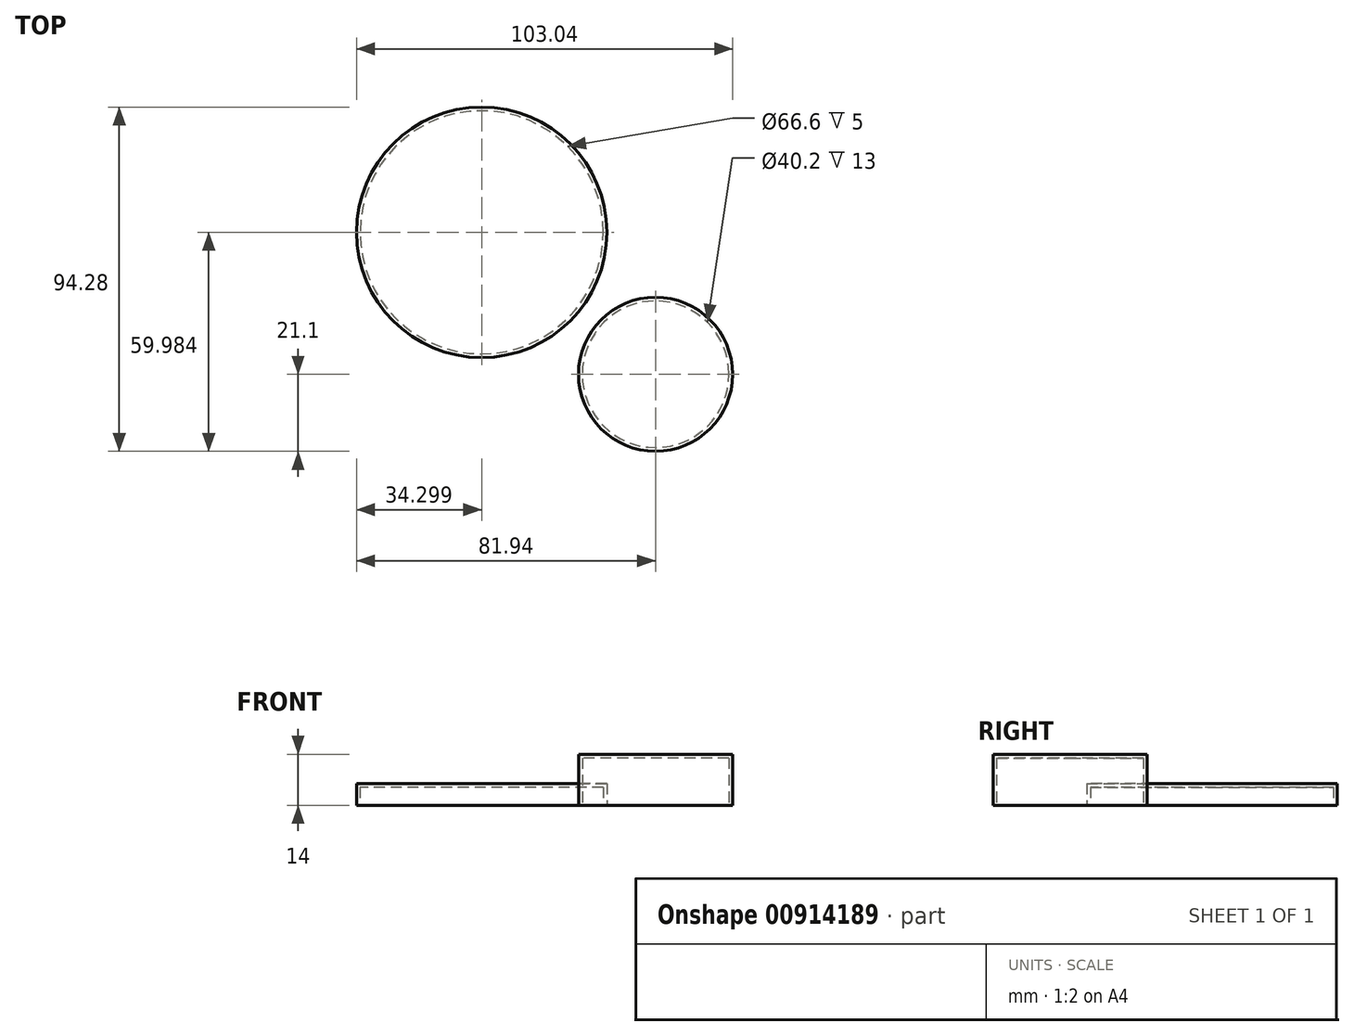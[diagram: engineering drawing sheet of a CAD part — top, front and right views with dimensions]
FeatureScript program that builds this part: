
annotation { "Feature Type Name" : "Feature", "Feature Type Description" : "" }
export const myFeature = defineFeature(function(context is Context, id is Id, definition is map)
    precondition{}
    {
        {
            assignVariable(context, id + "F0", {"name" : "height", "anyValue" : 14});
        }
        {
            assignVariable(context, id + "F1", {"name" : "height2", "anyValue" : 6});
        }
        {
            var Q0;
            Q0=qCreatedBy(makeId("Top.planeOp"),FACE);
            var sketch = newSketch(context, id + "F2", { "sketchPlane" : qUnion([Q0])});
            skCircle(sketch, "E0", {"center": v(0, 0) * mm, "radius": 20.1 * mm});
            skCircle(sketch, "E1", {"center": v(0, 0) * mm, "radius": 21.1 * mm});
            skLineSegment(sketch, "E2", {"start": v(0, 20.1) * mm, "end": v(0, 21.1) * mm, "construction": true});
            skCircle(sketch, "E3", {"center": v(-47.64, 38.88) * mm, "radius": 33.3 * mm});
            skCircle(sketch, "E4", {"center": v(-47.64, 38.88) * mm, "radius": 34.3 * mm});
            skLineSegment(sketch, "E5", {"start": v(-47.64, 72.18) * mm, "end": v(-47.64, 73.18) * mm, "construction": true});
            skSolve(sketch);
        }
        {
            var Q0;
            Q0=makeQuery(id+"F2.imprint","IMPRINT",FACE,{"disambiguationData":[TD([[makeQuery(id+"F2.imprint","IMPRINT",EDGE,{"derivedFrom":sQuery(id+"F2.wireOp",EDGE,"E0")}),-1.0]])]});
            var Q1;
            Q1=makeQuery(id+"F2.imprint","IMPRINT",FACE,{"disambiguationData":[TD([[makeQuery(id+"F2.imprint","IMPRINT",EDGE,{"derivedFrom":sQuery(id+"F2.wireOp",EDGE,"E0")}),1.0]])]});
            extrude(context, id + "F3", {"entities" : qUnion([Q0, Q1]), "depth" : (getVariable(context, 'height')) * mm, "offsetDistance" : 25 * mm});
        }
        {
            var Q0;
            Q0=makeQuery(id+"F2.imprint","IMPRINT",FACE,{"disambiguationData":[TD([[makeQuery(id+"F2.imprint","IMPRINT",EDGE,{"derivedFrom":sQuery(id+"F2.wireOp",EDGE,"E0")}),1.0]])]});
            extrude(context, id + "F4", {"entities" : qUnion([Q0]), "operationType" : NewBodyOperationType.REMOVE, "depth" : (getVariable(context, 'height') - 1) * mm, "offsetDistance" : 25 * mm});
        }
        {
            var Q0;
            Q0=makeQuery(id+"F2.imprint","IMPRINT",FACE,{"disambiguationData":[TD([[makeQuery(id+"F2.imprint","IMPRINT",EDGE,{"derivedFrom":sQuery(id+"F2.wireOp",EDGE,"E3")}),1.0]])]});
            var Q1;
            Q1=makeQuery(id+"F2.imprint","IMPRINT",FACE,{"disambiguationData":[TD([[makeQuery(id+"F2.imprint","IMPRINT",EDGE,{"derivedFrom":sQuery(id+"F2.wireOp",EDGE,"E3")}),-1.0]])]});
            var Q2;
            Q2=makeQuery(id+"F2.imprint","IMPRINT",FACE,{"disambiguationData":[TD([[makeQuery(id+"F2.imprint","IMPRINT",EDGE,{"derivedFrom":sQuery(id+"F2.wireOp",EDGE,"E3")}),1.0]])]});
            var Q3;
            Q3=makeQuery(id+"F2.imprint","IMPRINT",FACE,{"disambiguationData":[TD([[makeQuery(id+"F2.imprint","IMPRINT",EDGE,{"derivedFrom":sQuery(id+"F2.wireOp",EDGE,"E3")}),-1.0]])]});
            extrude(context, id + "F5", {"entities" : qUnion([Q0, Q1, Q2, Q3]), "depth" : (getVariable(context, 'height2')) * mm, "offsetDistance" : 25 * mm});
        }
        {
            var Q0;
            Q0=makeQuery(id+"F2.imprint","IMPRINT",FACE,{"disambiguationData":[TD([[makeQuery(id+"F2.imprint","IMPRINT",EDGE,{"derivedFrom":sQuery(id+"F2.wireOp",EDGE,"E3")}),1.0]])]});
            var Q1;
            Q1=makeQuery(id+"F2.imprint","IMPRINT",FACE,{"disambiguationData":[TD([[makeQuery(id+"F2.imprint","IMPRINT",EDGE,{"derivedFrom":sQuery(id+"F2.wireOp",EDGE,"E3")}),1.0]])]});
            extrude(context, id + "F6", {"entities" : qUnion([Q0, Q1]), "operationType" : NewBodyOperationType.REMOVE, "depth" : (getVariable(context, 'height2') - 1) * mm, "offsetDistance" : 25 * mm});
        }
    });
